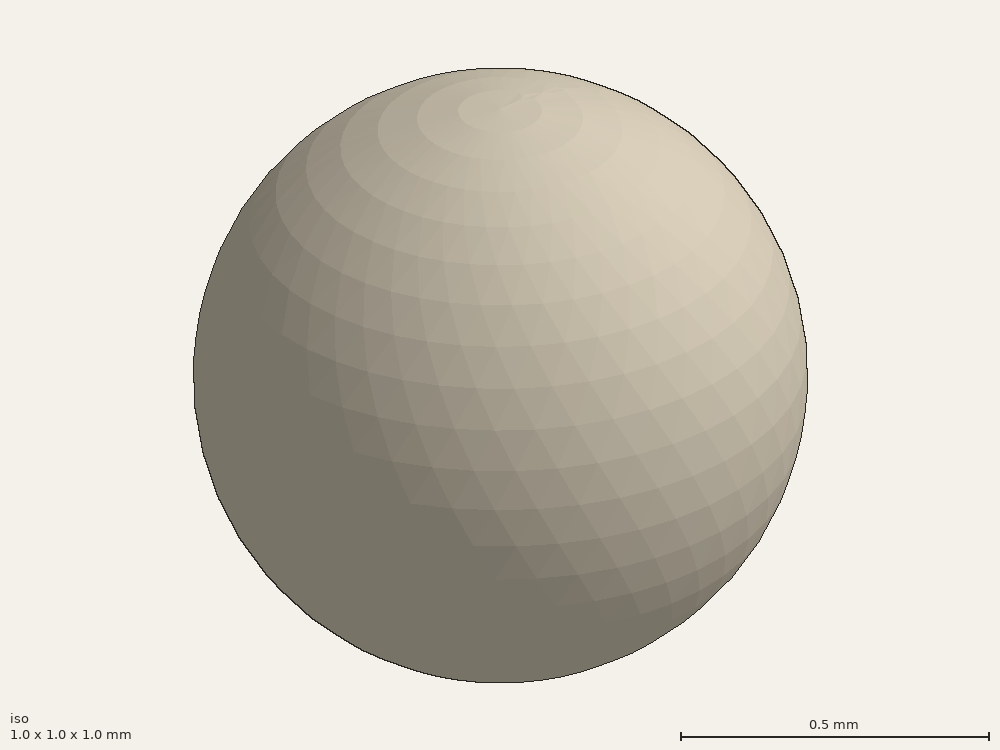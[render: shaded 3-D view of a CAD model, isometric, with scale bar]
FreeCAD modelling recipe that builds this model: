
FCSTD DOCUMENT  (FreeCAD 0.18R14555 (Git shallow))
Label: 146 - BALL COMB SPIRAL CIRC MOTION
License: All rights reserved
LicenseURL: http://en.wikipedia.org/wiki/All_rights_reserved
objects: App::DocumentObjectGroupPython×2, Part::Helix×1, Part::FeaturePython×1, Part::Sphere×1
note: 3 computed .brp shape members not serialized (recipe doc carries the construction recipe); baked Part::Feature solids carry a one-line shape summary decoded from their .brp

FEATURE [Part::Helix] Helix
  Angle = 0
  AttacherType = Attacher::AttachEngine3D
  Height = 2
  LocalCoord = 0
  Pitch = 2
  Placement = pos=(10,-2.2e-15,2.2e-15) rot=(-0.57735,0.57735,-0.57735;4.18879rad)
  Radius = 1
  Style = 1
FEATURE [Part::FeaturePython] Array  # Draft array (typed FeaturePython)
  Angle = 360
  ArrayType = 1
  Axis = (0,0,1)
  Base = -> Helix
  Center = (0,0,0)
  Fuse = false
  IntervalAxis = (0,0,0)
  IntervalX = (1,0,0)
  IntervalY = (0,1,0)
  IntervalZ = (0,0,1)
  NumberPolar = 32
  NumberX = 2
  NumberY = 2
  NumberZ = 1
FEATURE [Part::Sphere] Sphere
  Angle1 = -90
  Angle2 = 90
  Angle3 = 360
  AttacherType = Attacher::AttachEngine3D
  Placement = pos=(7.42345,7.90517,0.535827) rot=(0,0,1;0rad)
  Radius = 0.5
FEATURE [App::DocumentObjectGroupPython] My_Placer  # scripted group (container) (typed FeaturePython)
  Placement = pos=(7.42345,7.90517,0.535827) rot=(0,0,1;0rad)
  RotAxis = (0,0,1)
  RotCenter = (0,0,0)
  arc =  0
  arc0 = 0
  arc1 = 90
  target = -> Sphere
  time = 0.52
  x = x0
  x0 = 7.42345
  x1 = 200
  y = y0
  y0 = 7.90517
  y1 = 0
  z = z0
  z0 = 0.535827
  z1 = 0
  expr: z0 = cos(32 * time * 90)
  expr: y0 = (10 + sin(32 * time * 90)) * sin(time * 90)
  expr: x0 = (10 + sin(32 * time * 90)) * cos(time * 90)
FEATURE [App::DocumentObjectGroupPython] My_Manager  # scripted group (container) (typed FeaturePython)
  Group = -> [My_Placer]
  intervall = 400
  sleeptime = 0.02
  start = 0
  step = 53
  text = NO
